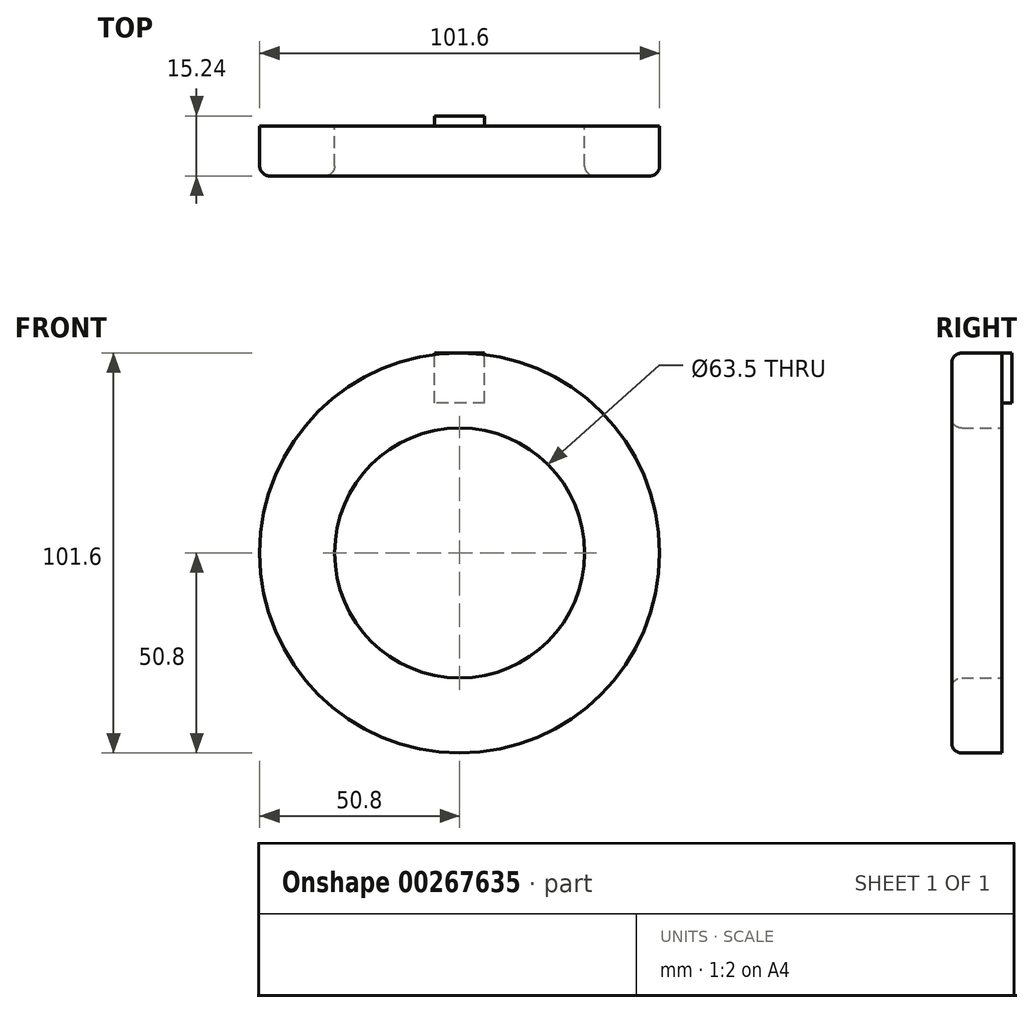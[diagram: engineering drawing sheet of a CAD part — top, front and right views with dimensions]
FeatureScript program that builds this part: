
annotation { "Feature Type Name" : "Feature", "Feature Type Description" : "" }
export const myFeature = defineFeature(function(context is Context, id is Id, definition is map)
    precondition{}
    {
        {
            var Q0;
            Q0=qCreatedBy(makeId("Front.planeOp"),FACE);
            var sketch = newSketch(context, id + "F0", { "sketchPlane" : qUnion([Q0])});
            skCircle(sketch, "E0", {"center": v(0, 0) * mm, "radius": 50.8 * mm});
            skCircle(sketch, "E1", {"center": v(0, 0) * mm, "radius": 31.75 * mm});
            skSolve(sketch);
        }
        {
            var Q0;
            Q0=makeQuery(id+"F0.imprint","IMPRINT",FACE,{"disambiguationData":[TD([[makeQuery(id+"F0.imprint","IMPRINT",EDGE,{"derivedFrom":sQuery(id+"F0.wireOp",EDGE,"E0")}),1.0]])]});
            extrude(context, id + "F1", {"entities" : qUnion([Q0]), "depth" : 12.7 * mm});
        }
        {
            var Q0;
            Q0=makeQuery(id+"F1.opExtrude","CAP_EDGE",EDGE,{"disambiguationData":[OSD([sQuery(id+"F0.wireOp",EDGE,"E0")])],"isStart":false});
            var Q1;
            Q1=makeQuery(id+"F1.opExtrude","CAP_EDGE",EDGE,{"disambiguationData":[OSD([sQuery(id+"F0.wireOp",EDGE,"E1")])],"isStart":false});
            fillet(context, id + "F2", {"entities" : qUnion([Q0, Q1]), "radius" : 2.54 * mm, "tangentPropagation" : true, "allowEdgeOverflow" : false});
        }
        {
            var Q0;
            Q0=qCreatedBy(makeId("Front.planeOp"),FACE);
            var sketch = newSketch(context, id + "F3", { "sketchPlane" : qUnion([Q0])});
            skLineSegment(sketch, "E2.bottom", {"start": v(6.35, 38.1) * mm, "end": v(-6.35, 38.1) * mm});
            skLineSegment(sketch, "E2.top", {"start": v(6.35, 50.8) * mm, "end": v(-6.35, 50.8) * mm});
            skLineSegment(sketch, "E2.left", {"start": v(6.35, 38.1) * mm, "end": v(6.35, 50.8) * mm});
            skLineSegment(sketch, "E2.right", {"start": v(-6.35, 38.1) * mm, "end": v(-6.35, 50.8) * mm});
            skSolve(sketch);
        }
        {
            var Q0;
            Q0 = qSketchRegion(id + "F3", true);
            extrude(context, id + "F4", {"entities" : qUnion([Q0]), "operationType" : NewBodyOperationType.ADD, "oppositeDirection" : true, "depth" : 2.54 * mm});
        }
    });
